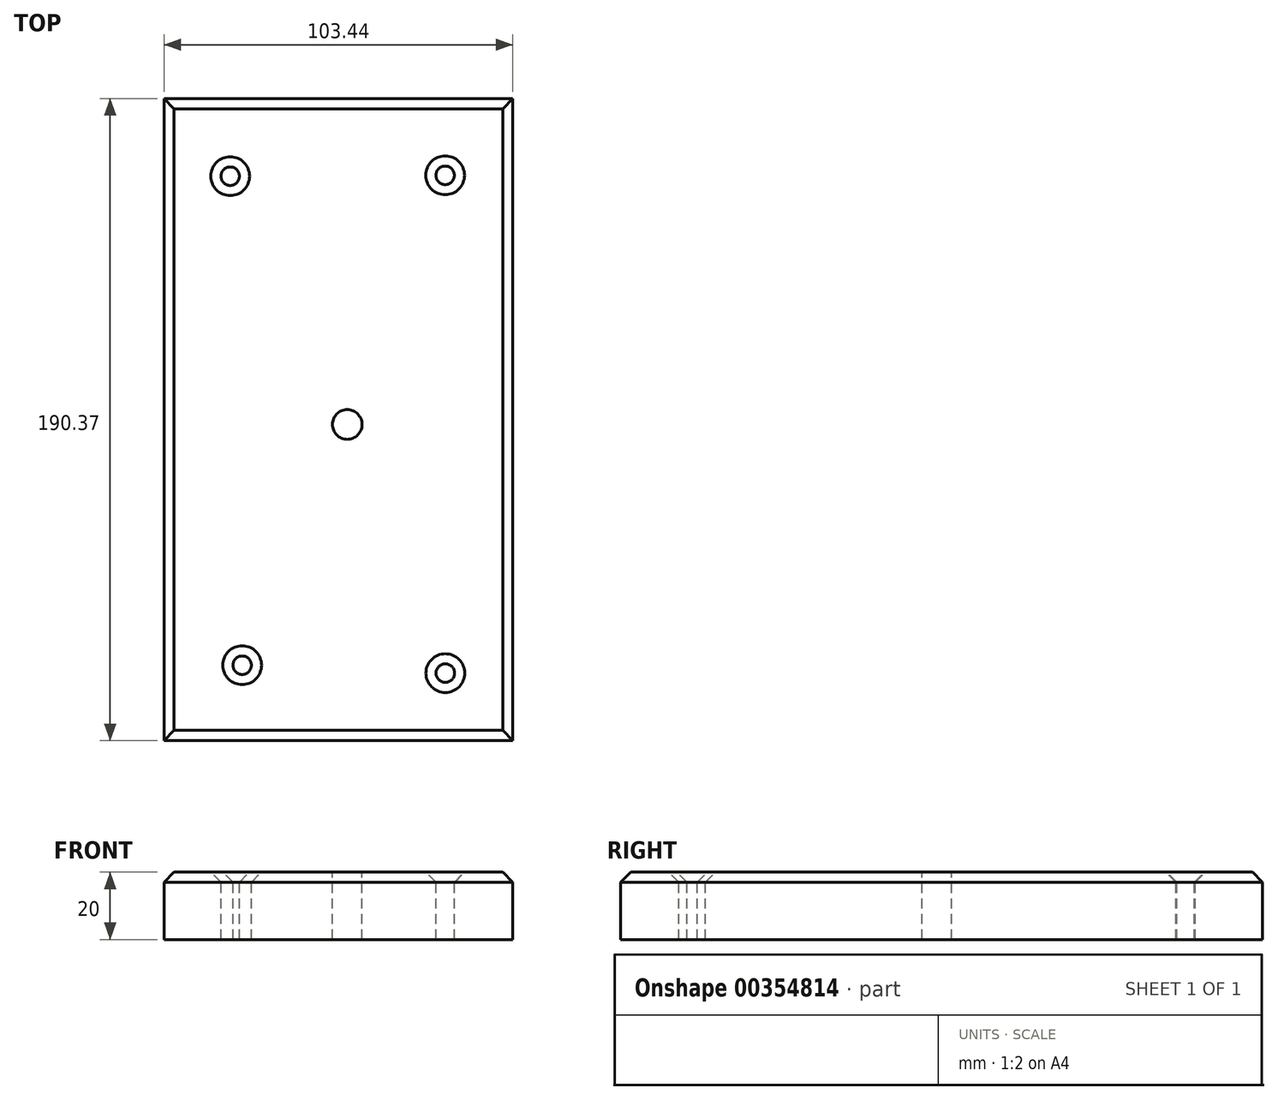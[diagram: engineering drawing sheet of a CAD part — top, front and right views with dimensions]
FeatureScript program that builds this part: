
annotation { "Feature Type Name" : "Feature", "Feature Type Description" : "" }
export const myFeature = defineFeature(function(context is Context, id is Id, definition is map)
    precondition{}
    {
        {
            var Q0;
            Q0=qCreatedBy(makeId("Top.planeOp"),FACE);
            var sketch = newSketch(context, id + "F0", { "sketchPlane" : qUnion([Q0])});
            skLineSegment(sketch, "E0.bottom", {"start": v(0, 0) * mm, "end": v(-103.44, 0) * mm});
            skLineSegment(sketch, "E0.top", {"start": v(0, 190.37) * mm, "end": v(-103.44, 190.37) * mm});
            skLineSegment(sketch, "E0.left", {"start": v(0, 0) * mm, "end": v(0, 190.37) * mm});
            skLineSegment(sketch, "E0.right", {"start": v(-103.44, 0) * mm, "end": v(-103.44, 190.37) * mm});
            skSolve(sketch);
        }
        {
            var Q0;
            Q0=makeQuery(id+"F0.imprint","IMPRINT",FACE,{"disambiguationData":[TD([[makeQuery(id+"F0.imprint","IMPRINT",EDGE,{"derivedFrom":sQuery(id+"F0.wireOp",EDGE,"E0.bottom")}),-1.0]])]});
            var Q1;
            Q1 = qSketchRegion(id + "F0", true);
            extrude(context, id + "F1", {"entities" : qUnion([Q0, Q1]), "depth" : 20 * mm});
        }
        {
            var Q0;
            Q0=makeQuery(id+"F1.opExtrude","CAP_FACE",FACE,{"disambiguationData":[OSD([sQuery(id+"F0.wireOp",EDGE,"E0.bottom"),sQuery(id+"F0.wireOp",EDGE,"E0.top"),sQuery(id+"F0.wireOp",EDGE,"E0.left"),sQuery(id+"F0.wireOp",EDGE,"E0.right")])],"isStart":false});
            var sketch = newSketch(context, id + "F2", { "sketchPlane" : qUnion([Q0])});
            skPoint(sketch, "E1", {"position": v(-20, 20) * mm});
            skPoint(sketch, "E2.0.1.0", {"position": v(-83.82, 167.39) * mm});
            skPoint(sketch, "E2.1.0.0", {"position": v(-20.07, 167.64) * mm});
            skPoint(sketch, "E2.1.1.0", {"position": v(-83.89, 315.03) * mm});
            skPoint(sketch, "E2.2.1.0", {"position": v(-83.95, 462.67) * mm});
            skPoint(sketch, "E3.1.0.0", {"position": v(-80.26, 22.35) * mm});
            skPoint(sketch, "E3.2.0.0", {"position": v(-140.53, 24.7) * mm});
            skLineSegment(sketch, "E3.direction1", {"start": v(-20, 20) * mm, "end": v(-80.26, 22.35) * mm, "construction": true});
            skSolve(sketch);
        }
        {
            var Q0;
            Q0=sQuery(id+"F2.wireOp",VERTEX,"ec997cf9-7f7e-4021-ad45-ec1017abc4a6");
            var Q1;
            Q1=sQuery(id+"F2.wireOp",VERTEX,"a9f244e7-be3b-4ee8-b15c-02df56e84092");
            var Q2;
            Q2=sQuery(id+"F2.wireOp",VERTEX,"5fb61200-ba63-4b89-9576-7f5e7e3bd700");
            var Q3;
            Q3=sQuery(id+"F2.wireOp",VERTEX,"E1");
            var Q4;
            Q4=sQuery(id+"F2.wireOp",VERTEX,"E2.0.1.0");
            var Q5;
            Q5=sQuery(id+"F2.wireOp",VERTEX,"E2.1.0.0");
            var Q6;
            Q6=sQuery(id+"F2.wireOp",VERTEX,"E3.1.0.0");
            var Q7;
            Q7=makeQuery(id+"F1.opExtrude","SWEPT_BODY",BODY,{"disambiguationData":[OSD([sQuery(id+"F0.wireOp",EDGE,"E0.bottom"),sQuery(id+"F0.wireOp",EDGE,"E0.top"),sQuery(id+"F0.wireOp",EDGE,"E0.left"),sQuery(id+"F0.wireOp",EDGE,"E0.right")])]});
            hole(context, id + "F3", {"style" : HoleStyle.SIMPLE, "endStyle" : HoleEndStyle.THROUGH, "standardTappedOrClearance" : lookupTablePath({ "standard" : "ISO", "fit" : "Normal", "size" : "M5", "type" : "Clearance" }), "standardBlindInLast" : lookupTablePath({ "fit" : "Standard", "standard" : "ISO", "size" : "M5", "type" : "Clearance" }), "holeDiameter" : 5.5 * mm, "isTappedThrough" : true, "tappedDepth" : 12.7 * mm, "tapClearance" : 3, "locations" : qUnion([Q0, Q1, Q2, Q3, Q4, Q5, Q6]), "scope" : qUnion([Q7])});
        }
        {
            var Q0;
            Q0=makeQuery(id+"F1.opExtrude","CAP_FACE",FACE,{"disambiguationData":[OSD([sQuery(id+"F0.wireOp",EDGE,"E0.bottom"),sQuery(id+"F0.wireOp",EDGE,"E0.top"),sQuery(id+"F0.wireOp",EDGE,"E0.left"),sQuery(id+"F0.wireOp",EDGE,"E0.right")])],"isStart":false});
            chamfer(context, id + "F4", {"entities" : qUnion([Q0]), "width" : 3 * mm, "tangentPropagation" : true});
        }
        {
            var Q0;
            Q0=makeQuery(id+"F1.opExtrude","CAP_FACE",FACE,{"disambiguationData":[OSD([sQuery(id+"F0.wireOp",EDGE,"E0.bottom"),sQuery(id+"F0.wireOp",EDGE,"E0.top"),sQuery(id+"F0.wireOp",EDGE,"E0.left"),sQuery(id+"F0.wireOp",EDGE,"E0.right")])],"isStart":false});
            var sketch = newSketch(context, id + "F5", { "sketchPlane" : qUnion([Q0])});
            skPoint(sketch, "E4", {"position": v(-49.1, 93.74) * mm});
            skSolve(sketch);
        }
        {
            var Q0;
            Q0=sQuery(id+"F5.wireOp",VERTEX,"E4");
            var Q1;
            Q1=makeQuery(id+"F1.opExtrude","SWEPT_BODY",BODY,{"disambiguationData":[OSD([sQuery(id+"F0.wireOp",EDGE,"E0.bottom"),sQuery(id+"F0.wireOp",EDGE,"E0.top"),sQuery(id+"F0.wireOp",EDGE,"E0.left"),sQuery(id+"F0.wireOp",EDGE,"E0.right")])]});
            hole(context, id + "F6", {"style" : HoleStyle.SIMPLE, "endStyle" : HoleEndStyle.THROUGH, "standardTappedOrClearance" : lookupTablePath({ "standard" : "ISO", "fit" : "Normal", "size" : "M8", "type" : "Clearance" }), "standardBlindInLast" : lookupTablePath({ "fit" : "Standard", "standard" : "ISO", "size" : "M8", "type" : "Clearance" }), "holeDiameter" : 8.8 * mm, "isTappedThrough" : true, "tappedDepth" : 12.7 * mm, "tapClearance" : 3, "locations" : qUnion([Q0]), "scope" : qUnion([Q1])});
        }
    });
